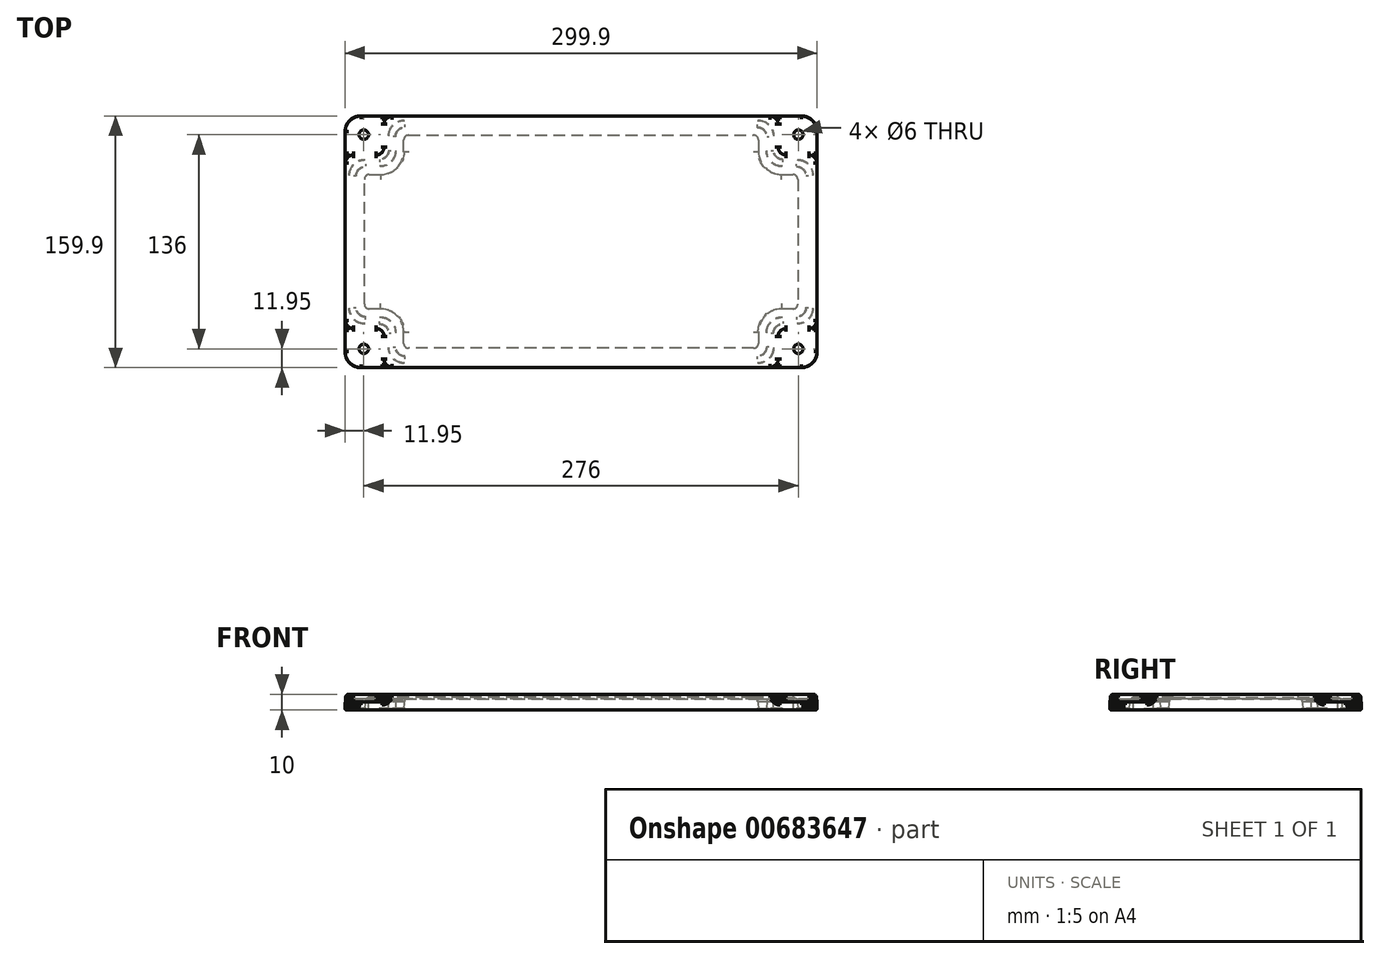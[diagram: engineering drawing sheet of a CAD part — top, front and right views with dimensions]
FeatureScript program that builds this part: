
annotation { "Feature Type Name" : "Feature", "Feature Type Description" : "" }
export const myFeature = defineFeature(function(context is Context, id is Id, definition is map)
    precondition{}
    {
        {
            var Q0;
            Q0=qCreatedBy(makeId("Front.planeOp"),FACE);
            cPlane(context, id + "F0", {"entities" : qUnion([Q0]), "cplaneType" : CPlaneType.OFFSET, "offset" : 80 * mm, "width" : 150 * mm, "height" : 150 * mm});
        }
        {
            var Q0;
            Q0=qCreatedBy(makeId("Right.planeOp"),FACE);
            cPlane(context, id + "F1", {"entities" : qUnion([Q0]), "cplaneType" : CPlaneType.OFFSET, "offset" : 150 * mm, "width" : 150 * mm, "height" : 150 * mm});
        }
        {
            var Q0;
            Q0=qCreatedBy(makeId("Top.planeOp"),FACE);
            var sketch = newSketch(context, id + "F2", { "sketchPlane" : qUnion([Q0])});
            skLineSegment(sketch, "E0.bottom", {"start": v(-150, 80) * mm, "end": v(150, 80) * mm});
            skLineSegment(sketch, "E0.top", {"start": v(-150, -80) * mm, "end": v(150, -80) * mm});
            skLineSegment(sketch, "E0.left", {"start": v(-150, 80) * mm, "end": v(-150, -80) * mm});
            skLineSegment(sketch, "E0.right", {"start": v(150, 80) * mm, "end": v(150, -80) * mm});
            skSolve(sketch);
        }
        {
            var Q0;
            Q0=makeQuery(id+"F2.imprint","IMPRINT",FACE,{"disambiguationData":[TD([[makeQuery(id+"F2.imprint","IMPRINT",EDGE,{"derivedFrom":sQuery(id+"F2.wireOp",EDGE,"E0.bottom")}),-1.0]])]});
            extrude(context, id + "F3", {"entities" : qUnion([Q0]), "depth" : 10 * mm, "offsetDistance" : 25 * mm, "hasDraft" : true, "draftAngle" : 3 * degree, "draftPullDirection" : true});
        }
        {
            var Q0;
            Q0=makeQuery(id+"F3.opExtrude","CAP_FACE",FACE,{"disambiguationData":[OSD([sQuery(id+"F2.wireOp",EDGE,"E0.bottom"),sQuery(id+"F2.wireOp",EDGE,"E0.top"),sQuery(id+"F2.wireOp",EDGE,"E0.left"),sQuery(id+"F2.wireOp",EDGE,"E0.right")])],"isStart":true});
            var sketch = newSketch(context, id + "F4", { "sketchPlane" : qUnion([Q0])});
            skLineSegment(sketch, "E1", {"start": v(0, 75) * mm, "end": v(120, 75) * mm});
            skLineSegment(sketch, "E2", {"start": v(120, 75) * mm, "end": v(120, 50) * mm});
            skLineSegment(sketch, "E3", {"start": v(120, 50) * mm, "end": v(145, 50) * mm});
            skLineSegment(sketch, "E4", {"start": v(145, 50) * mm, "end": v(145, 0) * mm});
            skLineSegment(sketch, "E5.MirrorCS", {"start": v(-120, 75) * mm, "end": v(-120, 50) * mm});
            skLineSegment(sketch, "E6.MirrorCS", {"start": v(0, 75) * mm, "end": v(-120, 75) * mm});
            skLineSegment(sketch, "E7.MirrorCS", {"start": v(-145, 50) * mm, "end": v(-145, 0) * mm});
            skLineSegment(sketch, "E8.MirrorCS", {"start": v(-120, 50) * mm, "end": v(-145, 50) * mm});
            skLineSegment(sketch, "E9.MirrorCS", {"start": v(0, -75) * mm, "end": v(120, -75) * mm});
            skLineSegment(sketch, "E10.MirrorCS", {"start": v(-120, -50) * mm, "end": v(-145, -50) * mm});
            skLineSegment(sketch, "E11.MirrorCS", {"start": v(-145, -50) * mm, "end": v(-145, 0) * mm});
            skLineSegment(sketch, "E12.MirrorCS", {"start": v(120, -50) * mm, "end": v(145, -50) * mm});
            skLineSegment(sketch, "E13.MirrorCS", {"start": v(0, -75) * mm, "end": v(-120, -75) * mm});
            skLineSegment(sketch, "E14.MirrorCS", {"start": v(-120, -75) * mm, "end": v(-120, -50) * mm});
            skLineSegment(sketch, "E15.MirrorCS", {"start": v(120, -75) * mm, "end": v(120, -50) * mm});
            skLineSegment(sketch, "E16.MirrorCS", {"start": v(145, -50) * mm, "end": v(145, 0) * mm});
            skSolve(sketch);
        }
        {
            var Q0;
            Q0=qCreatedBy(makeId("Right.planeOp"),FACE);
            var sketch = newSketch(context, id + "F5", { "sketchPlane" : qUnion([Q0])});
            skLineSegment(sketch, "E17.bottom", {"start": v(-77.47, -2) * mm, "end": v(-72.53, -2) * mm});
            skLineSegment(sketch, "E17.top", {"start": v(-77, 7) * mm, "end": v(-73, 7) * mm});
            skLineSegment(sketch, "E17.left", {"start": v(-77.47, -2) * mm, "end": v(-77, 7) * mm});
            skLineSegment(sketch, "E17.right", {"start": v(-72.53, -2) * mm, "end": v(-73, 7) * mm});
            skSolve(sketch);
        }
        {
            var Q0;
            Q0 = qSketchRegion(id + "F5", true);
            var Q1;
            Q1 = qConstructionFilter(qBodyType(qCreatedBy(id + "F4" ,EDGE), BodyType.WIRE), ConstructionObject.NO);
            sweep(context, id + "F6", {"operationType" : NewBodyOperationType.REMOVE, "profiles" : qUnion([Q0]), "path" : qUnion([Q1])});
        }
        {
            var Q0;
            Q0=makeQuery(id+"F2.imprint","IMPRINT",FACE,{"disambiguationData":[TD([[makeQuery(id+"F2.imprint","IMPRINT",EDGE,{"derivedFrom":sQuery(id+"F2.wireOp",EDGE,"E0.bottom")}),-1.0]])]});
            var sketch = newSketch(context, id + "F7", { "sketchPlane" : qUnion([Q0])});
            skLineSegment(sketch, "E18.0", {"start": v(117.63, -47.63) * mm, "end": v(117.63, -72.63) * mm, "construction": true});
            skLineSegment(sketch, "E18.1", {"start": v(117.63, -72.63) * mm, "end": v(-117.63, -72.63) * mm, "construction": true});
            skLineSegment(sketch, "E18.2", {"start": v(-117.63, -72.63) * mm, "end": v(-117.63, -47.63) * mm, "construction": true});
            skLineSegment(sketch, "E18.3", {"start": v(-117.63, -47.63) * mm, "end": v(-142.63, -47.63) * mm, "construction": true});
            skLineSegment(sketch, "E18.4", {"start": v(-142.63, -47.63) * mm, "end": v(-142.63, 47.63) * mm, "construction": true});
            skLineSegment(sketch, "E18.5", {"start": v(-142.63, 47.63) * mm, "end": v(-117.63, 47.63) * mm, "construction": true});
            skLineSegment(sketch, "E18.6", {"start": v(-117.63, 47.63) * mm, "end": v(-117.63, 72.63) * mm, "construction": true});
            skLineSegment(sketch, "E18.7", {"start": v(-117.63, 72.63) * mm, "end": v(117.63, 72.63) * mm, "construction": true});
            skLineSegment(sketch, "E18.8", {"start": v(117.63, 72.63) * mm, "end": v(117.63, 47.63) * mm, "construction": true});
            skLineSegment(sketch, "E18.9", {"start": v(117.63, 47.63) * mm, "end": v(142.63, 47.63) * mm, "construction": true});
            skLineSegment(sketch, "E18.10", {"start": v(142.63, 47.63) * mm, "end": v(142.63, -47.63) * mm, "construction": true});
            skLineSegment(sketch, "E18.11", {"start": v(142.63, -47.63) * mm, "end": v(117.63, -47.63) * mm, "construction": true});
            skLineSegment(sketch, "E19.0", {"start": v(137.63, -42.63) * mm, "end": v(112.63, -42.63) * mm});
            skLineSegment(sketch, "E19.1", {"start": v(-137.63, -42.63) * mm, "end": v(-137.63, 42.63) * mm});
            skLineSegment(sketch, "E19.2", {"start": v(-112.63, -42.63) * mm, "end": v(-137.63, -42.63) * mm});
            skLineSegment(sketch, "E19.3", {"start": v(-112.63, -67.63) * mm, "end": v(-112.63, -42.63) * mm});
            skLineSegment(sketch, "E19.4", {"start": v(112.63, -67.63) * mm, "end": v(-112.63, -67.63) * mm});
            skLineSegment(sketch, "E19.5", {"start": v(-137.63, 42.63) * mm, "end": v(-112.63, 42.63) * mm});
            skLineSegment(sketch, "E19.6", {"start": v(112.63, -42.63) * mm, "end": v(112.63, -67.63) * mm});
            skLineSegment(sketch, "E19.7", {"start": v(-112.63, 42.63) * mm, "end": v(-112.63, 67.63) * mm});
            skLineSegment(sketch, "E19.8", {"start": v(-112.63, 67.63) * mm, "end": v(112.63, 67.63) * mm});
            skLineSegment(sketch, "E19.9", {"start": v(112.63, 67.63) * mm, "end": v(112.63, 42.63) * mm});
            skLineSegment(sketch, "E19.10", {"start": v(112.63, 42.63) * mm, "end": v(137.63, 42.63) * mm});
            skLineSegment(sketch, "E19.11", {"start": v(137.63, 42.63) * mm, "end": v(137.63, -42.63) * mm});
            skSolve(sketch);
        }
        {
            var Q0;
            Q0 = qSketchRegion(id + "F7", true);
            extrude(context, id + "F8", {"entities" : qUnion([Q0]), "operationType" : NewBodyOperationType.REMOVE, "depth" : 8 * mm, "offsetDistance" : 25 * mm, "hasDraft" : true, "draftAngle" : 3 * degree, "draftPullDirection" : true});
        }
        {
            var Q0;
            Q0=makeQuery(id+"F3.opExtrude","CAP_FACE",FACE,{"disambiguationData":[OSD([sQuery(id+"F2.wireOp",EDGE,"E0.bottom"),sQuery(id+"F2.wireOp",EDGE,"E0.top"),sQuery(id+"F2.wireOp",EDGE,"E0.left"),sQuery(id+"F2.wireOp",EDGE,"E0.right")])],"isStart":false});
            var sketch = newSketch(context, id + "F9", { "sketchPlane" : qUnion([Q0])});
            skPoint(sketch, "E20", {"position": v(138, -68) * mm});
            skPoint(sketch, "E21.MirrorP", {"position": v(-138, -68) * mm});
            skPoint(sketch, "E22.MirrorP", {"position": v(-138, 68) * mm});
            skPoint(sketch, "E23.MirrorP", {"position": v(138, 68) * mm});
            skSolve(sketch);
        }
        {
            var Q0;
            Q0=makeQuery(id+"F3.opExtrude","CAP_FACE",FACE,{"disambiguationData":[OSD([sQuery(id+"F2.wireOp",EDGE,"E0.bottom"),sQuery(id+"F2.wireOp",EDGE,"E0.top"),sQuery(id+"F2.wireOp",EDGE,"E0.left"),sQuery(id+"F2.wireOp",EDGE,"E0.right")])],"isStart":false});
            var sketch = newSketch(context, id + "F10", { "sketchPlane" : qUnion([Q0])});
            skLineSegment(sketch, "E24.bottom", {"start": v(125, -55) * mm, "end": v(155, -55) * mm});
            skLineSegment(sketch, "E24.top", {"start": v(125, -85) * mm, "end": v(155, -85) * mm});
            skLineSegment(sketch, "E24.left", {"start": v(125, -55) * mm, "end": v(125, -85) * mm});
            skLineSegment(sketch, "E24.right", {"start": v(155, -55) * mm, "end": v(155, -85) * mm});
            skLineSegment(sketch, "E25.MirrorCS", {"start": v(155, 55) * mm, "end": v(155, 85) * mm});
            skLineSegment(sketch, "E26.MirrorCS", {"start": v(125, 85) * mm, "end": v(155, 85) * mm});
            skLineSegment(sketch, "E27.MirrorCS", {"start": v(125, 55) * mm, "end": v(125, 85) * mm});
            skLineSegment(sketch, "E28.MirrorCS", {"start": v(125, 55) * mm, "end": v(155, 55) * mm});
            skLineSegment(sketch, "E29.MirrorCS", {"start": v(-155, 55) * mm, "end": v(-155, 85) * mm});
            skLineSegment(sketch, "E30.MirrorCS", {"start": v(-125, 55) * mm, "end": v(-155, 55) * mm});
            skLineSegment(sketch, "E31.MirrorCS", {"start": v(-125, -85) * mm, "end": v(-155, -85) * mm});
            skLineSegment(sketch, "E32.MirrorCS", {"start": v(-125, 85) * mm, "end": v(-155, 85) * mm});
            skLineSegment(sketch, "E33.MirrorCS", {"start": v(-125, -55) * mm, "end": v(-125, -85) * mm});
            skLineSegment(sketch, "E34.MirrorCS", {"start": v(-125, 55) * mm, "end": v(-125, 85) * mm});
            skLineSegment(sketch, "E35.MirrorCS", {"start": v(-155, -55) * mm, "end": v(-155, -85) * mm});
            skLineSegment(sketch, "E36.MirrorCS", {"start": v(-125, -55) * mm, "end": v(-155, -55) * mm});
            skSolve(sketch);
        }
        {
            var Q0;
            {var subQ5=sQuery(id+"F10.wireOp",EDGE,"E29.MirrorCS");Q0=makeQuery(id+"F10.imprint","IMPRINT",FACE,{"disambiguationData":[TD([[makeQuery(id+"F10.imprint","IMPRINT",EDGE,{"derivedFrom":subQ5}),-1.0]])]});}
            var Q1;
            {var subQ0=sQuery(id+"F10.wireOp",EDGE,"E34.MirrorCS");var subQ1=sQuery(id+"F10.wireOp",EDGE,"E30.MirrorCS");var subQ2=makeQuery(id+"F10.imprint","INTERSECT",VERTEX,{"derivedFrom":[subQ1,subQ0]});Q1=makeQuery(id+"F10.imprint","IMPRINT",FACE,{"disambiguationData":[TD([[makeQuery(id+"F10.imprint","IMPRINT",EDGE,{"disambiguationData":[TD([[subQ2,-1.0]])],"derivedFrom":subQ1}),-1.0]])]});}
            var Q2;
            {var subQ0=sQuery(id+"F10.wireOp",EDGE,"E36.MirrorCS");var subQ1=sQuery(id+"F10.wireOp",EDGE,"E33.MirrorCS");var subQ2=makeQuery(id+"F10.imprint","INTERSECT",VERTEX,{"derivedFrom":[subQ1,subQ0]});Q2=makeQuery(id+"F10.imprint","IMPRINT",FACE,{"disambiguationData":[TD([[makeQuery(id+"F10.imprint","IMPRINT",EDGE,{"disambiguationData":[TD([[subQ2,-1.0]])],"derivedFrom":subQ1}),-1.0]])]});}
            var Q3;
            {var subQ5=sQuery(id+"F10.wireOp",EDGE,"E31.MirrorCS");Q3=makeQuery(id+"F10.imprint","IMPRINT",FACE,{"disambiguationData":[TD([[makeQuery(id+"F10.imprint","IMPRINT",EDGE,{"derivedFrom":subQ5}),-1.0]])]});}
            var Q4;
            {var subQ0=sQuery(id+"F10.wireOp",EDGE,"E24.left");var subQ1=sQuery(id+"F10.wireOp",EDGE,"E24.bottom");var subQ2=makeQuery(id+"F10.imprint","INTERSECT",VERTEX,{"derivedFrom":[subQ1,subQ0]});Q4=makeQuery(id+"F10.imprint","IMPRINT",FACE,{"disambiguationData":[TD([[makeQuery(id+"F10.imprint","IMPRINT",EDGE,{"disambiguationData":[TD([[subQ2,-1.0]])],"derivedFrom":subQ1}),-1.0]])]});}
            var Q5;
            {var subQ2=sQuery(id+"F10.wireOp",EDGE,"E24.top");Q5=makeQuery(id+"F10.imprint","IMPRINT",FACE,{"disambiguationData":[TD([[makeQuery(id+"F10.imprint","IMPRINT",EDGE,{"derivedFrom":subQ2}),1.0]])]});}
            var Q6;
            {var subQ5=sQuery(id+"F10.wireOp",EDGE,"E25.MirrorCS");Q6=makeQuery(id+"F10.imprint","IMPRINT",FACE,{"disambiguationData":[TD([[makeQuery(id+"F10.imprint","IMPRINT",EDGE,{"derivedFrom":subQ5}),1.0]])]});}
            var Q7;
            {var subQ0=sQuery(id+"F10.wireOp",EDGE,"E28.MirrorCS");var subQ1=sQuery(id+"F10.wireOp",EDGE,"E27.MirrorCS");var subQ2=makeQuery(id+"F10.imprint","INTERSECT",VERTEX,{"derivedFrom":[subQ1,subQ0]});Q7=makeQuery(id+"F10.imprint","IMPRINT",FACE,{"disambiguationData":[TD([[makeQuery(id+"F10.imprint","IMPRINT",EDGE,{"disambiguationData":[TD([[subQ2,-1.0]])],"derivedFrom":subQ1}),-1.0]])]});}
            extrude(context, id + "F11", {"entities" : qUnion([Q0, Q1, Q2, Q3, Q4, Q5, Q6, Q7]), "operationType" : NewBodyOperationType.REMOVE, "oppositeDirection" : true, "depth" : 5 * mm, "offsetDistance" : 25 * mm, "hasDraft" : true, "draftAngle" : 3 * degree, "draftPullDirection" : true});
        }
        {
            var Q0;
            Q0=sQuery(id+"F9.wireOp",VERTEX,"E20");
            var Q1;
            Q1=sQuery(id+"F9.wireOp",VERTEX,"E23.MirrorP");
            var Q2;
            Q2=sQuery(id+"F9.wireOp",VERTEX,"E22.MirrorP");
            var Q3;
            Q3=sQuery(id+"F9.wireOp",VERTEX,"E21.MirrorP");
            var Q4;
            Q4=makeQuery(id+"F3.opExtrude","SWEPT_BODY",BODY,{"disambiguationData":[OSD([sQuery(id+"F2.wireOp",EDGE,"E0.bottom"),sQuery(id+"F2.wireOp",EDGE,"E0.top"),sQuery(id+"F2.wireOp",EDGE,"E0.left"),sQuery(id+"F2.wireOp",EDGE,"E0.right")])]});
            hole(context, id + "F12", {"style" : HoleStyle.SIMPLE, "endStyle" : HoleEndStyle.THROUGH, "holeDiameter" : 6 * mm, "majorDiameter" : 6 * mm, "tappedDepth" : 12 * mm, "tapClearance" : 3, "locations" : qUnion([Q0, Q1, Q2, Q3]), "scope" : qUnion([Q4])});
        }
        {
            var Q0;
            Q0=makeQuery(id+"F3.opExtrude","SWEPT_EDGE",EDGE,{"disambiguationData":[OSD([sQuery(id+"F2.wireOp",EDGE,"E0.bottom"),sQuery(id+"F2.wireOp",EDGE,"E0.right")])]});
            var Q1;
            Q1=makeQuery(id+"F3.opExtrude","SWEPT_EDGE",EDGE,{"disambiguationData":[OSD([sQuery(id+"F2.wireOp",EDGE,"E0.bottom"),sQuery(id+"F2.wireOp",EDGE,"E0.left")])]});
            var Q2;
            Q2=makeQuery(id+"F3.opExtrude","SWEPT_EDGE",EDGE,{"disambiguationData":[OSD([sQuery(id+"F2.wireOp",EDGE,"E0.top"),sQuery(id+"F2.wireOp",EDGE,"E0.right")])]});
            var Q3;
            Q3=makeQuery(id+"F3.opExtrude","SWEPT_EDGE",EDGE,{"disambiguationData":[OSD([sQuery(id+"F2.wireOp",EDGE,"E0.top"),sQuery(id+"F2.wireOp",EDGE,"E0.left")])]});
            fillet(context, id + "F13", {"entities" : qUnion([Q0, Q1, Q2, Q3]), "radius" : 10 * mm, "tangentPropagation" : true, "allowEdgeOverflow" : false});
        }
        {
            var Q0;
            Q0=makeQuery(id+"F11.boolean.opBoolean","INTERSECT",EDGE,{"derivedFrom":[makeQuery(id+"F3.opExtrude","SWEPT_FACE",FACE,{"disambiguationData":[OSD([sQuery(id+"F2.wireOp",EDGE,"E0.left")])]}),makeQuery(id+"F11.opExtrude","SWEPT_FACE",FACE,{"disambiguationData":[OSD([sQuery(id+"F10.wireOp",EDGE,"E36.MirrorCS")])]})]});
            var Q1;
            Q1=makeQuery(id+"F11.boolean.opBoolean","COPY",EDGE,{"derivedFrom":makeQuery(id+"F11.opExtrude","SWEPT_EDGE",EDGE,{"disambiguationData":[OSD([sQuery(id+"F10.wireOp",EDGE,"E33.MirrorCS"),sQuery(id+"F10.wireOp",EDGE,"E36.MirrorCS")])]})});
            var Q2;
            Q2=makeQuery(id+"F11.boolean.opBoolean","INTERSECT",EDGE,{"derivedFrom":[makeQuery(id+"F3.opExtrude","SWEPT_FACE",FACE,{"disambiguationData":[OSD([sQuery(id+"F2.wireOp",EDGE,"E0.top")])]}),makeQuery(id+"F11.opExtrude","SWEPT_FACE",FACE,{"disambiguationData":[OSD([sQuery(id+"F10.wireOp",EDGE,"E33.MirrorCS")])]})]});
            var Q3;
            Q3=makeQuery(id+"F11.boolean.opBoolean","INTERSECT",EDGE,{"derivedFrom":[makeQuery(id+"F3.opExtrude","SWEPT_FACE",FACE,{"disambiguationData":[OSD([sQuery(id+"F2.wireOp",EDGE,"E0.left")])]}),makeQuery(id+"F11.opExtrude","SWEPT_FACE",FACE,{"disambiguationData":[OSD([sQuery(id+"F10.wireOp",EDGE,"E30.MirrorCS")])]})]});
            var Q4;
            Q4=makeQuery(id+"F11.boolean.opBoolean","INTERSECT",EDGE,{"derivedFrom":[makeQuery(id+"F3.opExtrude","SWEPT_FACE",FACE,{"disambiguationData":[OSD([sQuery(id+"F2.wireOp",EDGE,"E0.bottom")])]}),makeQuery(id+"F11.opExtrude","SWEPT_FACE",FACE,{"disambiguationData":[OSD([sQuery(id+"F10.wireOp",EDGE,"E34.MirrorCS")])]})]});
            var Q5;
            Q5=makeQuery(id+"F11.boolean.opBoolean","COPY",EDGE,{"derivedFrom":makeQuery(id+"F11.opExtrude","SWEPT_EDGE",EDGE,{"disambiguationData":[OSD([sQuery(id+"F10.wireOp",EDGE,"E30.MirrorCS"),sQuery(id+"F10.wireOp",EDGE,"E34.MirrorCS")])]})});
            var Q6;
            Q6=makeQuery(id+"F11.boolean.opBoolean","INTERSECT",EDGE,{"derivedFrom":[makeQuery(id+"F3.opExtrude","SWEPT_FACE",FACE,{"disambiguationData":[OSD([sQuery(id+"F2.wireOp",EDGE,"E0.top")])]}),makeQuery(id+"F11.opExtrude","SWEPT_FACE",FACE,{"disambiguationData":[OSD([sQuery(id+"F10.wireOp",EDGE,"E24.left")])]})]});
            var Q7;
            Q7=makeQuery(id+"F11.boolean.opBoolean","COPY",EDGE,{"derivedFrom":makeQuery(id+"F11.opExtrude","SWEPT_EDGE",EDGE,{"disambiguationData":[OSD([sQuery(id+"F10.wireOp",EDGE,"E24.bottom"),sQuery(id+"F10.wireOp",EDGE,"E24.left")])]})});
            var Q8;
            Q8=makeQuery(id+"F11.boolean.opBoolean","INTERSECT",EDGE,{"derivedFrom":[makeQuery(id+"F3.opExtrude","SWEPT_FACE",FACE,{"disambiguationData":[OSD([sQuery(id+"F2.wireOp",EDGE,"E0.right")])]}),makeQuery(id+"F11.opExtrude","SWEPT_FACE",FACE,{"disambiguationData":[OSD([sQuery(id+"F10.wireOp",EDGE,"E24.bottom")])]})]});
            var Q9;
            Q9=makeQuery(id+"F11.boolean.opBoolean","INTERSECT",EDGE,{"derivedFrom":[makeQuery(id+"F3.opExtrude","SWEPT_FACE",FACE,{"disambiguationData":[OSD([sQuery(id+"F2.wireOp",EDGE,"E0.right")])]}),makeQuery(id+"F11.opExtrude","SWEPT_FACE",FACE,{"disambiguationData":[OSD([sQuery(id+"F10.wireOp",EDGE,"E28.MirrorCS")])]})]});
            var Q10;
            Q10=makeQuery(id+"F11.boolean.opBoolean","COPY",EDGE,{"derivedFrom":makeQuery(id+"F11.opExtrude","SWEPT_EDGE",EDGE,{"disambiguationData":[OSD([sQuery(id+"F10.wireOp",EDGE,"E27.MirrorCS"),sQuery(id+"F10.wireOp",EDGE,"E28.MirrorCS")])]})});
            var Q11;
            Q11=makeQuery(id+"F11.boolean.opBoolean","INTERSECT",EDGE,{"derivedFrom":[makeQuery(id+"F3.opExtrude","SWEPT_FACE",FACE,{"disambiguationData":[OSD([sQuery(id+"F2.wireOp",EDGE,"E0.bottom")])]}),makeQuery(id+"F11.opExtrude","SWEPT_FACE",FACE,{"disambiguationData":[OSD([sQuery(id+"F10.wireOp",EDGE,"E27.MirrorCS")])]})]});
            fillet(context, id + "F14", {"entities" : qUnion([Q0, Q1, Q2, Q3, Q4, Q5, Q6, Q7, Q8, Q9, Q10, Q11]), "radius" : 5 * mm, "tangentPropagation" : true, "allowEdgeOverflow" : false});
        }
        {
            var Q0;
            Q0=makeQuery(id+"F6.boolean.opBoolean","COPY",EDGE,{"derivedFrom":makeQuery(id+"F6.opSweep","MID_CAP_EDGE",EDGE,{"disambiguationData":[OSD([sQuery(id+"F4.wireOp",VERTEX,"E14.MirrorCS.end"),sQuery(id+"F5.wireOp",EDGE,"E17.right")])],"capPos":10.0})});
            var Q1;
            Q1=makeQuery(id+"F6.boolean.opBoolean","COPY",EDGE,{"derivedFrom":makeQuery(id+"F6.opSweep","MID_CAP_EDGE",EDGE,{"disambiguationData":[OSD([sQuery(id+"F4.wireOp",VERTEX,"E8.MirrorCS.start"),sQuery(id+"F5.wireOp",EDGE,"E17.right")])],"capPos":14.0})});
            var Q2;
            Q2=makeQuery(id+"F6.boolean.opBoolean","COPY",EDGE,{"derivedFrom":makeQuery(id+"F6.opSweep","MID_CAP_EDGE",EDGE,{"disambiguationData":[OSD([sQuery(id+"F4.wireOp",VERTEX,"E14.MirrorCS.start"),sQuery(id+"F5.wireOp",EDGE,"E17.left")])],"capPos":9.0})});
            var Q3;
            Q3=makeQuery(id+"F6.boolean.opBoolean","COPY",EDGE,{"derivedFrom":makeQuery(id+"F6.opSweep","MID_CAP_EDGE",EDGE,{"disambiguationData":[OSD([sQuery(id+"F4.wireOp",VERTEX,"E11.MirrorCS.start"),sQuery(id+"F5.wireOp",EDGE,"E17.left")])],"capPos":11.0})});
            var Q4;
            Q4=makeQuery(id+"F6.boolean.opBoolean","COPY",EDGE,{"derivedFrom":makeQuery(id+"F6.opSweep","MID_CAP_EDGE",EDGE,{"disambiguationData":[OSD([sQuery(id+"F4.wireOp",VERTEX,"E3.start"),sQuery(id+"F5.wireOp",EDGE,"E17.right")])],"capPos":2.0})});
            var Q5;
            Q5=makeQuery(id+"F6.boolean.opBoolean","COPY",EDGE,{"derivedFrom":makeQuery(id+"F6.opSweep","MID_CAP_EDGE",EDGE,{"disambiguationData":[OSD([sQuery(id+"F4.wireOp",VERTEX,"E6.MirrorCS.end"),sQuery(id+"F5.wireOp",EDGE,"E17.left")])],"capPos":15.0})});
            var Q6;
            Q6=makeQuery(id+"F6.boolean.opBoolean","COPY",EDGE,{"derivedFrom":makeQuery(id+"F6.opSweep","MID_CAP_EDGE",EDGE,{"disambiguationData":[OSD([sQuery(id+"F4.wireOp",VERTEX,"E8.MirrorCS.end"),sQuery(id+"F5.wireOp",EDGE,"E17.left")])],"capPos":13.0})});
            var Q7;
            Q7=makeQuery(id+"F6.boolean.opBoolean","COPY",EDGE,{"derivedFrom":makeQuery(id+"F6.opSweep","MID_CAP_EDGE",EDGE,{"disambiguationData":[OSD([sQuery(id+"F4.wireOp",VERTEX,"E2.start"),sQuery(id+"F5.wireOp",EDGE,"E17.left")])],"capPos":1.0})});
            var Q8;
            Q8=makeQuery(id+"F6.boolean.opBoolean","COPY",EDGE,{"derivedFrom":makeQuery(id+"F6.opSweep","MID_CAP_EDGE",EDGE,{"disambiguationData":[OSD([sQuery(id+"F4.wireOp",VERTEX,"E4.start"),sQuery(id+"F5.wireOp",EDGE,"E17.left")])],"capPos":3.0})});
            var Q9;
            Q9=makeQuery(id+"F6.boolean.opBoolean","COPY",EDGE,{"derivedFrom":makeQuery(id+"F6.opSweep","MID_CAP_EDGE",EDGE,{"disambiguationData":[OSD([sQuery(id+"F4.wireOp",VERTEX,"E15.MirrorCS.start"),sQuery(id+"F5.wireOp",EDGE,"E17.left")])],"capPos":7.0})});
            var Q10;
            Q10=makeQuery(id+"F6.boolean.opBoolean","COPY",EDGE,{"derivedFrom":makeQuery(id+"F6.opSweep","MID_CAP_EDGE",EDGE,{"disambiguationData":[OSD([sQuery(id+"F4.wireOp",VERTEX,"E16.MirrorCS.start"),sQuery(id+"F5.wireOp",EDGE,"E17.left")])],"capPos":5.0})});
            var Q11;
            Q11=makeQuery(id+"F6.boolean.opBoolean","COPY",EDGE,{"derivedFrom":makeQuery(id+"F6.opSweep","MID_CAP_EDGE",EDGE,{"disambiguationData":[OSD([sQuery(id+"F4.wireOp",VERTEX,"E15.MirrorCS.end"),sQuery(id+"F5.wireOp",EDGE,"E17.right")])],"capPos":6.0})});
            fillet(context, id + "F15", {"entities" : qUnion([Q0, Q1, Q2, Q3, Q4, Q5, Q6, Q7, Q8, Q9, Q10, Q11]), "radius" : 10 * mm, "tangentPropagation" : true, "allowEdgeOverflow" : false});
        }
        {
            var Q0;
            Q0=makeQuery(id+"F6.boolean.opBoolean","COPY",EDGE,{"derivedFrom":makeQuery(id+"F6.opSweep","MID_CAP_EDGE",EDGE,{"disambiguationData":[OSD([sQuery(id+"F4.wireOp",VERTEX,"E16.MirrorCS.start"),sQuery(id+"F5.wireOp",EDGE,"E17.right")])],"capPos":5.0})});
            var Q1;
            Q1=makeQuery(id+"F6.boolean.opBoolean","COPY",EDGE,{"derivedFrom":makeQuery(id+"F6.opSweep","MID_CAP_EDGE",EDGE,{"disambiguationData":[OSD([sQuery(id+"F4.wireOp",VERTEX,"E4.start"),sQuery(id+"F5.wireOp",EDGE,"E17.right")])],"capPos":3.0})});
            var Q2;
            Q2=makeQuery(id+"F6.boolean.opBoolean","COPY",EDGE,{"derivedFrom":makeQuery(id+"F6.opSweep","MID_CAP_EDGE",EDGE,{"disambiguationData":[OSD([sQuery(id+"F4.wireOp",VERTEX,"E2.start"),sQuery(id+"F5.wireOp",EDGE,"E17.right")])],"capPos":1.0})});
            var Q3;
            Q3=makeQuery(id+"F6.boolean.opBoolean","COPY",EDGE,{"derivedFrom":makeQuery(id+"F6.opSweep","MID_CAP_EDGE",EDGE,{"disambiguationData":[OSD([sQuery(id+"F4.wireOp",VERTEX,"E11.MirrorCS.start"),sQuery(id+"F5.wireOp",EDGE,"E17.right")])],"capPos":11.0})});
            var Q4;
            Q4=makeQuery(id+"F6.boolean.opBoolean","COPY",EDGE,{"derivedFrom":makeQuery(id+"F6.opSweep","MID_CAP_EDGE",EDGE,{"disambiguationData":[OSD([sQuery(id+"F4.wireOp",VERTEX,"E14.MirrorCS.start"),sQuery(id+"F5.wireOp",EDGE,"E17.right")])],"capPos":9.0})});
            var Q5;
            Q5=makeQuery(id+"F6.boolean.opBoolean","COPY",EDGE,{"derivedFrom":makeQuery(id+"F6.opSweep","MID_CAP_EDGE",EDGE,{"disambiguationData":[OSD([sQuery(id+"F4.wireOp",VERTEX,"E8.MirrorCS.end"),sQuery(id+"F5.wireOp",EDGE,"E17.right")])],"capPos":13.0})});
            var Q6;
            Q6=makeQuery(id+"F6.boolean.opBoolean","COPY",EDGE,{"derivedFrom":makeQuery(id+"F6.opSweep","MID_CAP_EDGE",EDGE,{"disambiguationData":[OSD([sQuery(id+"F4.wireOp",VERTEX,"E6.MirrorCS.end"),sQuery(id+"F5.wireOp",EDGE,"E17.right")])],"capPos":15.0})});
            var Q7;
            Q7=makeQuery(id+"F6.boolean.opBoolean","COPY",EDGE,{"derivedFrom":makeQuery(id+"F6.opSweep","MID_CAP_EDGE",EDGE,{"disambiguationData":[OSD([sQuery(id+"F4.wireOp",VERTEX,"E15.MirrorCS.end"),sQuery(id+"F5.wireOp",EDGE,"E17.left")])],"capPos":6.0})});
            var Q8;
            Q8=makeQuery(id+"F6.boolean.opBoolean","COPY",EDGE,{"derivedFrom":makeQuery(id+"F6.opSweep","MID_CAP_EDGE",EDGE,{"disambiguationData":[OSD([sQuery(id+"F4.wireOp",VERTEX,"E8.MirrorCS.start"),sQuery(id+"F5.wireOp",EDGE,"E17.left")])],"capPos":14.0})});
            var Q9;
            Q9=makeQuery(id+"F6.boolean.opBoolean","COPY",EDGE,{"derivedFrom":makeQuery(id+"F6.opSweep","MID_CAP_EDGE",EDGE,{"disambiguationData":[OSD([sQuery(id+"F4.wireOp",VERTEX,"E3.start"),sQuery(id+"F5.wireOp",EDGE,"E17.left")])],"capPos":2.0})});
            var Q10;
            Q10=makeQuery(id+"F6.boolean.opBoolean","COPY",EDGE,{"derivedFrom":makeQuery(id+"F6.opSweep","MID_CAP_EDGE",EDGE,{"disambiguationData":[OSD([sQuery(id+"F4.wireOp",VERTEX,"E15.MirrorCS.start"),sQuery(id+"F5.wireOp",EDGE,"E17.right")])],"capPos":7.0})});
            var Q11;
            Q11=makeQuery(id+"F6.boolean.opBoolean","COPY",EDGE,{"derivedFrom":makeQuery(id+"F6.opSweep","MID_CAP_EDGE",EDGE,{"disambiguationData":[OSD([sQuery(id+"F4.wireOp",VERTEX,"E14.MirrorCS.end"),sQuery(id+"F5.wireOp",EDGE,"E17.left")])],"capPos":10.0})});
            fillet(context, id + "F16", {"entities" : qUnion([Q0, Q1, Q2, Q3, Q4, Q5, Q6, Q7, Q8, Q9, Q10, Q11]), "radius" : 6 * mm, "tangentPropagation" : true, "allowEdgeOverflow" : false});
        }
        {
            var Q0;
            Q0=makeQuery(id+"F8.boolean.opBoolean","COPY",EDGE,{"derivedFrom":makeQuery(id+"F8.opExtrude","SWEPT_EDGE",EDGE,{"disambiguationData":[OSD([sQuery(id+"F7.wireOp",EDGE,"E19.4"),sQuery(id+"F7.wireOp",EDGE,"E19.6")])]})});
            var Q1;
            Q1=makeQuery(id+"F8.boolean.opBoolean","COPY",EDGE,{"derivedFrom":makeQuery(id+"F8.opExtrude","SWEPT_EDGE",EDGE,{"disambiguationData":[OSD([sQuery(id+"F7.wireOp",EDGE,"E19.0"),sQuery(id+"F7.wireOp",EDGE,"E19.11")])]})});
            var Q2;
            Q2=makeQuery(id+"F8.boolean.opBoolean","COPY",EDGE,{"derivedFrom":makeQuery(id+"F8.opExtrude","SWEPT_EDGE",EDGE,{"disambiguationData":[OSD([sQuery(id+"F7.wireOp",EDGE,"E19.1"),sQuery(id+"F7.wireOp",EDGE,"E19.2")])]})});
            var Q3;
            Q3=makeQuery(id+"F8.boolean.opBoolean","COPY",EDGE,{"derivedFrom":makeQuery(id+"F8.opExtrude","SWEPT_EDGE",EDGE,{"disambiguationData":[OSD([sQuery(id+"F7.wireOp",EDGE,"E19.3"),sQuery(id+"F7.wireOp",EDGE,"E19.4")])]})});
            var Q4;
            Q4=makeQuery(id+"F8.boolean.opBoolean","COPY",EDGE,{"derivedFrom":makeQuery(id+"F8.opExtrude","SWEPT_EDGE",EDGE,{"disambiguationData":[OSD([sQuery(id+"F7.wireOp",EDGE,"E19.8"),sQuery(id+"F7.wireOp",EDGE,"E19.9")])]})});
            var Q5;
            Q5=makeQuery(id+"F8.boolean.opBoolean","COPY",EDGE,{"derivedFrom":makeQuery(id+"F8.opExtrude","SWEPT_EDGE",EDGE,{"disambiguationData":[OSD([sQuery(id+"F7.wireOp",EDGE,"E19.10"),sQuery(id+"F7.wireOp",EDGE,"E19.11")])]})});
            var Q6;
            Q6=makeQuery(id+"F8.boolean.opBoolean","COPY",EDGE,{"derivedFrom":makeQuery(id+"F8.opExtrude","SWEPT_EDGE",EDGE,{"disambiguationData":[OSD([sQuery(id+"F7.wireOp",EDGE,"E19.7"),sQuery(id+"F7.wireOp",EDGE,"E19.8")])]})});
            var Q7;
            Q7=makeQuery(id+"F8.boolean.opBoolean","COPY",EDGE,{"derivedFrom":makeQuery(id+"F8.opExtrude","SWEPT_EDGE",EDGE,{"disambiguationData":[OSD([sQuery(id+"F7.wireOp",EDGE,"E19.1"),sQuery(id+"F7.wireOp",EDGE,"E19.5")])]})});
            fillet(context, id + "F17", {"entities" : qUnion([Q0, Q1, Q2, Q3, Q4, Q5, Q6, Q7]), "radius" : 3 * mm, "tangentPropagation" : true, "allowEdgeOverflow" : false});
        }
        {
            var Q0;
            Q0=makeQuery(id+"F8.boolean.opBoolean","COPY",EDGE,{"derivedFrom":makeQuery(id+"F8.opExtrude","SWEPT_EDGE",EDGE,{"disambiguationData":[OSD([sQuery(id+"F7.wireOp",EDGE,"E19.0"),sQuery(id+"F7.wireOp",EDGE,"E19.6")])]})});
            var Q1;
            Q1=makeQuery(id+"F8.boolean.opBoolean","COPY",EDGE,{"derivedFrom":makeQuery(id+"F8.opExtrude","SWEPT_EDGE",EDGE,{"disambiguationData":[OSD([sQuery(id+"F7.wireOp",EDGE,"E19.9"),sQuery(id+"F7.wireOp",EDGE,"E19.10")])]})});
            var Q2;
            Q2=makeQuery(id+"F8.boolean.opBoolean","COPY",EDGE,{"derivedFrom":makeQuery(id+"F8.opExtrude","SWEPT_EDGE",EDGE,{"disambiguationData":[OSD([sQuery(id+"F7.wireOp",EDGE,"E19.2"),sQuery(id+"F7.wireOp",EDGE,"E19.3")])]})});
            var Q3;
            Q3=makeQuery(id+"F8.boolean.opBoolean","COPY",EDGE,{"derivedFrom":makeQuery(id+"F8.opExtrude","SWEPT_EDGE",EDGE,{"disambiguationData":[OSD([sQuery(id+"F7.wireOp",EDGE,"E19.5"),sQuery(id+"F7.wireOp",EDGE,"E19.7")])]})});
            fillet(context, id + "F18", {"entities" : qUnion([Q0, Q1, Q2, Q3]), "radius" : 15 * mm, "tangentPropagation" : true, "allowEdgeOverflow" : false});
        }
        {
            var Q0;
            Q0=makeQuery(id+"F3.opExtrude","CAP_EDGE",EDGE,{"disambiguationData":[OSD([sQuery(id+"F2.wireOp",EDGE,"E0.bottom")])],"isStart":true});
            var Q1;
            Q1=makeQuery(id+"F6.boolean.opBoolean","INTERSECT",EDGE,{"derivedFrom":[makeQuery(id+"F3.opExtrude","CAP_FACE",FACE,{"disambiguationData":[OSD([sQuery(id+"F2.wireOp",EDGE,"E0.bottom"),sQuery(id+"F2.wireOp",EDGE,"E0.top"),sQuery(id+"F2.wireOp",EDGE,"E0.left"),sQuery(id+"F2.wireOp",EDGE,"E0.right")])],"isStart":true}),makeQuery(id+"F6.opSweep","SWEPT_FACE",FACE,{"disambiguationData":[OSD([sQuery(id+"F4.wireOp",EDGE,"E13.MirrorCS"),sQuery(id+"F5.wireOp",EDGE,"E17.left")])]})]});
            var Q2;
            Q2=makeQuery(id+"F6.boolean.opBoolean","INTERSECT",EDGE,{"derivedFrom":[makeQuery(id+"F3.opExtrude","CAP_FACE",FACE,{"disambiguationData":[OSD([sQuery(id+"F2.wireOp",EDGE,"E0.bottom"),sQuery(id+"F2.wireOp",EDGE,"E0.top"),sQuery(id+"F2.wireOp",EDGE,"E0.left"),sQuery(id+"F2.wireOp",EDGE,"E0.right")])],"isStart":true}),makeQuery(id+"F6.opSweep","SWEPT_FACE",FACE,{"disambiguationData":[OSD([sQuery(id+"F4.wireOp",EDGE,"E13.MirrorCS"),sQuery(id+"F5.wireOp",EDGE,"E17.right")])]})]});
            var Q3;
            Q3=makeQuery(id+"F8.boolean.opBoolean","COPY",EDGE,{"derivedFrom":makeQuery(id+"F8.opExtrude","CAP_EDGE",EDGE,{"disambiguationData":[OSD([sQuery(id+"F7.wireOp",EDGE,"E19.8")])],"isStart":true})});
            fillet(context, id + "F19", {"entities" : qUnion([Q0, Q1, Q2, Q3]), "radius" : 1 * mm, "tangentPropagation" : true, "allowEdgeOverflow" : false});
        }
        {
            var Q0;
            Q0=makeQuery(id+"F6.boolean.opBoolean","COPY",FACE,{"derivedFrom":makeQuery(id+"F6.opSweep","SWEPT_FACE",FACE,{"disambiguationData":[OSD([sQuery(id+"F4.wireOp",EDGE,"E2"),sQuery(id+"F5.wireOp",EDGE,"E17.top")])]})});
            fillet(context, id + "F20", {"entities" : qUnion([Q0]), "radius" : 1.5 * mm, "tangentPropagation" : true, "allowEdgeOverflow" : false});
        }
        {
            var Q0;
            Q0=makeQuery(id+"F8.boolean.opBoolean","COPY",EDGE,{"derivedFrom":makeQuery(id+"F8.opExtrude","CAP_EDGE",EDGE,{"disambiguationData":[OSD([sQuery(id+"F7.wireOp",EDGE,"E19.4")])],"isStart":false})});
            fillet(context, id + "F21", {"entities" : qUnion([Q0]), "radius" : 3 * mm, "tangentPropagation" : true, "allowEdgeOverflow" : false});
        }
        {
            var Q0;
            Q0=makeQuery(id+"F3.opExtrude","CAP_EDGE",EDGE,{"disambiguationData":[OSD([sQuery(id+"F2.wireOp",EDGE,"E0.right")])],"isStart":false});
            var Q1;
            Q1=makeQuery(id+"F13.opFillet","BLEND_EDGE",EDGE,{"blendedFrom":[makeQuery(id+"F3.opExtrude","SWEPT_EDGE",EDGE,{"disambiguationData":[OSD([sQuery(id+"F2.wireOp",EDGE,"E0.top"),sQuery(id+"F2.wireOp",EDGE,"E0.right")])]}),makeQuery(id+"F11.boolean.opBoolean","COPY",FACE,{"derivedFrom":makeQuery(id+"F11.opExtrude","CAP_FACE",FACE,{"disambiguationData":[OSD([sQuery(id+"F10.wireOp",EDGE,"E24.bottom"),sQuery(id+"F10.wireOp",EDGE,"E24.top"),sQuery(id+"F10.wireOp",EDGE,"E24.left"),sQuery(id+"F10.wireOp",EDGE,"E24.right")])],"isStart":false})})],"blendedInto":[makeQuery(id+"F11.boolean.opBoolean","COPY",FACE,{"derivedFrom":makeQuery(id+"F11.opExtrude","CAP_FACE",FACE,{"disambiguationData":[OSD([sQuery(id+"F10.wireOp",EDGE,"E24.bottom"),sQuery(id+"F10.wireOp",EDGE,"E24.top"),sQuery(id+"F10.wireOp",EDGE,"E24.left"),sQuery(id+"F10.wireOp",EDGE,"E24.right")])],"isStart":false})})]});
            var Q2;
            {var subQ0=sQuery(id+"F10.wireOp",EDGE,"E24.left");var subQ1=sQuery(id+"F10.wireOp",EDGE,"E24.bottom");Q2=makeQuery(id+"F14.opFillet","BLEND_EDGE",EDGE,{"blendedFrom":[makeQuery(id+"F11.boolean.opBoolean","COPY",EDGE,{"derivedFrom":makeQuery(id+"F11.opExtrude","SWEPT_EDGE",EDGE,{"disambiguationData":[OSD([subQ1,subQ0])]})}),makeQuery(id+"F11.boolean.opBoolean","COPY",FACE,{"derivedFrom":makeQuery(id+"F11.opExtrude","CAP_FACE",FACE,{"disambiguationData":[OSD([subQ1,sQuery(id+"F10.wireOp",EDGE,"E24.top"),subQ0,sQuery(id+"F10.wireOp",EDGE,"E24.right")])],"isStart":false})})],"blendedInto":[makeQuery(id+"F11.boolean.opBoolean","COPY",FACE,{"derivedFrom":makeQuery(id+"F11.opExtrude","CAP_FACE",FACE,{"disambiguationData":[OSD([subQ1,sQuery(id+"F10.wireOp",EDGE,"E24.top"),subQ0,sQuery(id+"F10.wireOp",EDGE,"E24.right")])],"isStart":false})})]});}
            var Q3;
            Q3=makeQuery(id+"F11.boolean.opBoolean","COPY",EDGE,{"derivedFrom":makeQuery(id+"F11.opExtrude","CAP_EDGE",EDGE,{"disambiguationData":[OSD([sQuery(id+"F10.wireOp",EDGE,"E36.MirrorCS")])],"isStart":false})});
            var Q4;
            Q4=makeQuery(id+"F11.boolean.opBoolean","INTERSECT",EDGE,{"derivedFrom":[makeQuery(id+"F3.opExtrude","SWEPT_FACE",FACE,{"disambiguationData":[OSD([sQuery(id+"F2.wireOp",EDGE,"E0.top")])]}),makeQuery(id+"F11.opExtrude","CAP_FACE",FACE,{"disambiguationData":[OSD([sQuery(id+"F10.wireOp",EDGE,"E31.MirrorCS"),sQuery(id+"F10.wireOp",EDGE,"E33.MirrorCS"),sQuery(id+"F10.wireOp",EDGE,"E35.MirrorCS"),sQuery(id+"F10.wireOp",EDGE,"E36.MirrorCS")])],"isStart":false})]});
            var Q5;
            Q5=makeQuery(id+"F11.boolean.opBoolean","COPY",EDGE,{"derivedFrom":makeQuery(id+"F11.opExtrude","CAP_EDGE",EDGE,{"disambiguationData":[OSD([sQuery(id+"F10.wireOp",EDGE,"E27.MirrorCS")])],"isStart":false})});
            var Q6;
            Q6=makeQuery(id+"F11.boolean.opBoolean","INTERSECT",EDGE,{"derivedFrom":[makeQuery(id+"F3.opExtrude","SWEPT_FACE",FACE,{"disambiguationData":[OSD([sQuery(id+"F2.wireOp",EDGE,"E0.right")])]}),makeQuery(id+"F11.opExtrude","CAP_FACE",FACE,{"disambiguationData":[OSD([sQuery(id+"F10.wireOp",EDGE,"E25.MirrorCS"),sQuery(id+"F10.wireOp",EDGE,"E26.MirrorCS"),sQuery(id+"F10.wireOp",EDGE,"E27.MirrorCS"),sQuery(id+"F10.wireOp",EDGE,"E28.MirrorCS")])],"isStart":false})]});
            var Q7;
            Q7=makeQuery(id+"F11.boolean.opBoolean","COPY",EDGE,{"derivedFrom":makeQuery(id+"F11.opExtrude","CAP_EDGE",EDGE,{"disambiguationData":[OSD([sQuery(id+"F10.wireOp",EDGE,"E30.MirrorCS")])],"isStart":false})});
            var Q8;
            Q8=makeQuery(id+"F11.boolean.opBoolean","INTERSECT",EDGE,{"derivedFrom":[makeQuery(id+"F3.opExtrude","SWEPT_FACE",FACE,{"disambiguationData":[OSD([sQuery(id+"F2.wireOp",EDGE,"E0.bottom")])]}),makeQuery(id+"F11.opExtrude","CAP_FACE",FACE,{"disambiguationData":[OSD([sQuery(id+"F10.wireOp",EDGE,"E29.MirrorCS"),sQuery(id+"F10.wireOp",EDGE,"E30.MirrorCS"),sQuery(id+"F10.wireOp",EDGE,"E32.MirrorCS"),sQuery(id+"F10.wireOp",EDGE,"E34.MirrorCS")])],"isStart":false})]});
            fillet(context, id + "F22", {"entities" : qUnion([Q0, Q1, Q2, Q3, Q4, Q5, Q6, Q7, Q8]), "radius" : 2 * mm, "tangentPropagation" : true, "allowEdgeOverflow" : false});
        }
    });
